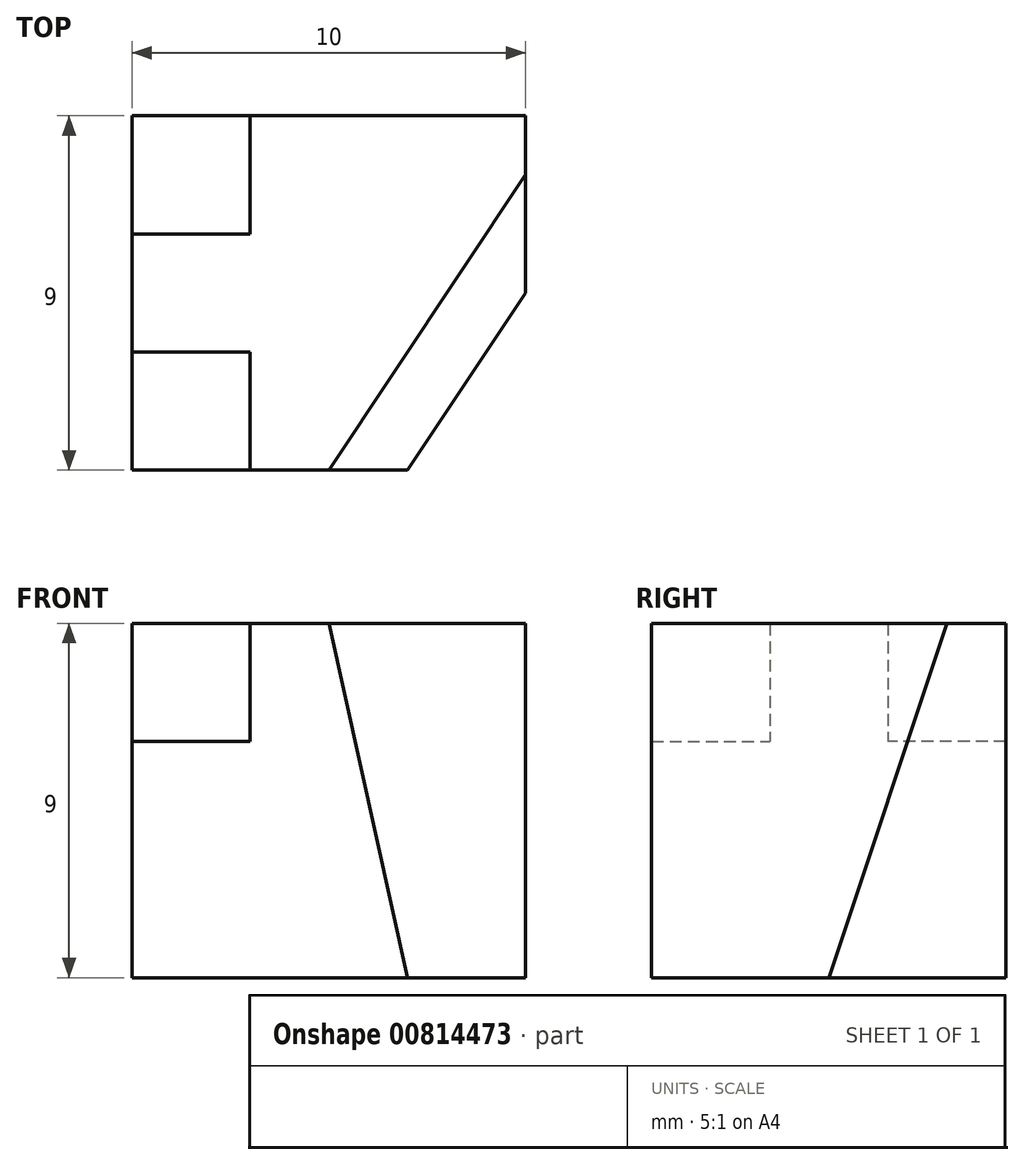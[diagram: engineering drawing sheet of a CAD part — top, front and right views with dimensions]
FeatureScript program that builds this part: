
annotation { "Feature Type Name" : "Feature", "Feature Type Description" : "" }
export const myFeature = defineFeature(function(context is Context, id is Id, definition is map)
    precondition{}
    {
        {
            var Q0;
            Q0=qCreatedBy(makeId("Right.planeOp"),FACE);
            var sketch = newSketch(context, id + "F0", { "sketchPlane" : qUnion([Q0])});
            skLineSegment(sketch, "E0.bottom", {"start": v(0, 0) * mm, "end": v(9, 0) * mm});
            skLineSegment(sketch, "E0.top", {"start": v(0, 9) * mm, "end": v(9, 9) * mm});
            skLineSegment(sketch, "E0.left", {"start": v(0, 0) * mm, "end": v(0, 9) * mm});
            skLineSegment(sketch, "E0.right", {"start": v(9, 0) * mm, "end": v(9, 9) * mm});
            skLineSegment(sketch, "E1.bottom", {"start": v(0, 9) * mm, "end": v(3, 9) * mm});
            skLineSegment(sketch, "E1.top", {"start": v(0, 6) * mm, "end": v(3, 6) * mm});
            skLineSegment(sketch, "E1.left", {"start": v(0, 9) * mm, "end": v(0, 6) * mm});
            skLineSegment(sketch, "E1.right", {"start": v(3, 9) * mm, "end": v(3, 6) * mm});
            skLineSegment(sketch, "E2.bottom", {"start": v(9, 9) * mm, "end": v(6, 9) * mm});
            skLineSegment(sketch, "E2.top", {"start": v(9, 6) * mm, "end": v(6, 6) * mm});
            skLineSegment(sketch, "E2.left", {"start": v(9, 9) * mm, "end": v(9, 6) * mm});
            skLineSegment(sketch, "E2.right", {"start": v(6, 9) * mm, "end": v(6, 6) * mm});
            skSolve(sketch);
        }
        {
            var Q0;
            {var subQ1=sQuery(id+"F0.wireOp",EDGE,"E0.bottom");var subQ2=sQuery(id+"F0.wireOp",EDGE,"E1.top");var subQ5=sQuery(id+"F0.wireOp",EDGE,"E2.top");var subQ13=makeQuery(id+"F0.imprint","IMPRINT",EDGE,{"derivedFrom":subQ2});var subQ15=makeQuery(id+"F0.imprint","IMPRINT",EDGE,{"derivedFrom":subQ5});Q0=qUnion([makeQuery(id+"F0.imprint","IMPRINT",FACE,{"disambiguationData":[TD([[subQ15,-1.0]])]}),makeQuery(id+"F0.imprint","IMPRINT",FACE,{"disambiguationData":[TD([[subQ13,1.0]])]}),makeQuery(id+"F0.imprint","IMPRINT",FACE,{"disambiguationData":[TD([[makeQuery(id+"F0.imprint","IMPRINT",EDGE,{"derivedFrom":subQ1}),1.0]])]})]);}
            extrude(context, id + "F1", {"entities" : qUnion([Q0]), "depth" : 10 * mm, "offsetDistance" : 25 * mm});
        }
        {
            var Q0;
            {var subQ4=sQuery(id+"F0.wireOp",EDGE,"E2.top");Q0=makeQuery(id+"F0.imprint","IMPRINT",FACE,{"disambiguationData":[TD([[makeQuery(id+"F0.imprint","IMPRINT",EDGE,{"derivedFrom":subQ4}),-1.0]])]});}
            var Q1;
            {var subQ4=sQuery(id+"F0.wireOp",EDGE,"E1.top");Q1=makeQuery(id+"F0.imprint","IMPRINT",FACE,{"disambiguationData":[TD([[makeQuery(id+"F0.imprint","IMPRINT",EDGE,{"derivedFrom":subQ4}),1.0]])]});}
            extrude(context, id + "F2", {"entities" : qUnion([Q0, Q1]), "operationType" : NewBodyOperationType.REMOVE, "depth" : 3 * mm, "offsetDistance" : 25 * mm});
        }
        {
            var Q0;
            Q0=makeQuery(id+"F1.opExtrude","SWEPT_FACE",FACE,{"disambiguationData":[OSD([sQuery(id+"F0.wireOp",EDGE,"E0.left")])]});
            var sketch = newSketch(context, id + "F3", { "sketchPlane" : qUnion([Q0])});
            skPoint(sketch, "E3", {"position": v(7, 0) * mm});
            skPoint(sketch, "E4", {"position": v(5, 9) * mm});
            skSolve(sketch);
        }
        {
            var Q0;
            Q0=makeQuery(id+"F1.opExtrude","CAP_EDGE",EDGE,{"disambiguationData":[OSD([sQuery(id+"F0.wireOp",EDGE,"E0.bottom")])],"isStart":false});
            cPoint(context, id + "F4", {"entities" : qUnion([Q0]), "parameter" : 0.5});
        }
        {
            var Q0;
            Q0=sQuery(id+"F3.wireOp",VERTEX,"E4");
            var Q1;
            Q1=sQuery(id+"F3.wireOp",VERTEX,"E3");
            var Q2;
            Q2 = qCreatedBy(id + "F4" ,VERTEX);
            cPlane(context, id + "F5", {"entities" : qUnion([Q0, Q1, Q2]), "cplaneType" : CPlaneType.THREE_POINT, "offset" : 25 * mm, "width" : 150 * mm, "height" : 150 * mm});
        }
        {
            var Q0;
            Q0=qCreatedBy(id+"F5.planeOp",FACE);
            var sketch = newSketch(context, id + "F6", { "sketchPlane" : qUnion([Q0])});
            skLineSegment(sketch, "E5", {"start": v(-3.73, 7.7) * mm, "end": v(-12.68, 6.62) * mm});
            skLineSegment(sketch, "E6", {"start": v(-12.68, 6.62) * mm, "end": v(-7.97, -4.94) * mm});
            skLineSegment(sketch, "E7", {"start": v(-3.73, -4.42) * mm, "end": v(-3.73, 7.7) * mm});
            skLineSegment(sketch, "E8", {"start": v(-3.73, -1.52) * mm, "end": v(-9.1, -2.17) * mm});
            skPoint(sketch, "E9.orphan", {"position": v(-3.73, -1.52) * mm});
            skPoint(sketch, "E10.orphan", {"position": v(-9.1, -2.17) * mm});
            skLineSegment(sketch, "E11", {"start": v(-3.73, -4.42) * mm, "end": v(-7.97, -4.94) * mm});
            skSolve(sketch);
        }
        {
            var Q0;
            Q0 = qSketchRegion(id + "F6", true);
            extrude(context, id + "F7", {"entities" : qUnion([Q0]), "operationType" : NewBodyOperationType.REMOVE, "endBound" : BoundingType.THROUGH_ALL, "oppositeDirection" : true, "depth" : 25 * mm, "offsetDistance" : 25 * mm});
        }
        {
            var Q0;
            Q0=makeQuery(id+"F1.opExtrude","SWEPT_FACE",FACE,{"disambiguationData":[OSD([sQuery(id+"F0.wireOp",EDGE,"E0.left")])]});
            cPlane(context, id + "F8", {"entities" : qUnion([Q0]), "cplaneType" : CPlaneType.OFFSET, "offset" : 4.5 * mm, "oppositeDirection" : true, "width" : 150 * mm, "height" : 150 * mm});
        }
    });
